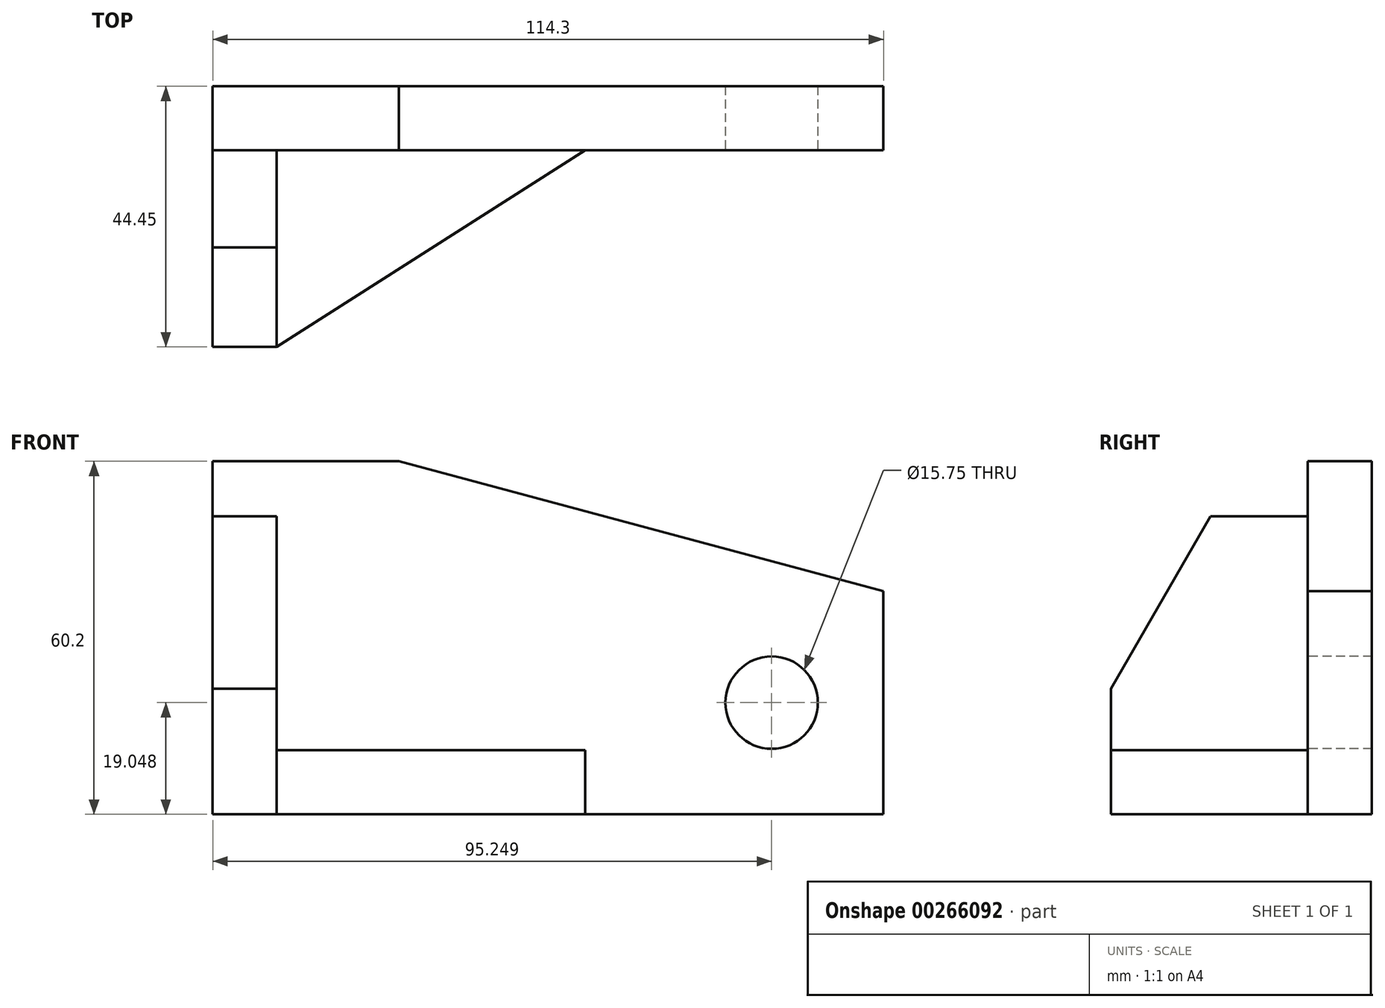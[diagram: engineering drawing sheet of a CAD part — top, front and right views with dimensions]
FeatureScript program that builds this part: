
annotation { "Feature Type Name" : "Feature", "Feature Type Description" : "" }
export const myFeature = defineFeature(function(context is Context, id is Id, definition is map)
    precondition{}
    {
        {
            var Q0;
            Q0=qCreatedBy(makeId("Front.planeOp"),FACE);
            var sketch = newSketch(context, id + "F0", { "sketchPlane" : qUnion([Q0])});
            skLineSegment(sketch, "E0.bottom", {"start": v(-55.92, 20.43) * mm, "end": v(58.38, 20.43) * mm});
            skLineSegment(sketch, "E0.top", {"start": v(-55.92, -39.77) * mm, "end": v(58.38, -39.77) * mm});
            skLineSegment(sketch, "E0.left", {"start": v(-55.92, 20.43) * mm, "end": v(-55.92, -39.77) * mm});
            skLineSegment(sketch, "E0.right", {"start": v(58.38, 20.43) * mm, "end": v(58.38, -39.77) * mm});
            skSolve(sketch);
        }
        {
            var Q0;
            Q0 = qSketchRegion(id + "F0", true);
            extrude(context, id + "F1", {"entities" : qUnion([Q0]), "depth" : 10.92 * mm});
        }
        {
            var Q0;
            Q0=makeQuery(id+"F1.opExtrude","CAP_FACE",FACE,{"disambiguationData":[OSD([sQuery(id+"F0.wireOp",EDGE,"E0.bottom"),sQuery(id+"F0.wireOp",EDGE,"E0.top"),sQuery(id+"F0.wireOp",EDGE,"E0.left"),sQuery(id+"F0.wireOp",EDGE,"E0.right")])],"isStart":false});
            var sketch = newSketch(context, id + "F2", { "sketchPlane" : qUnion([Q0])});
            skLineSegment(sketch, "E1", {"start": v(58.38, 20.43) * mm, "end": v(-24.17, 20.43) * mm});
            skLineSegment(sketch, "E2", {"start": v(58.38, 20.43) * mm, "end": v(58.38, -1.7) * mm});
            skLineSegment(sketch, "E3", {"start": v(58.38, -1.7) * mm, "end": v(-24.17, 20.43) * mm});
            skSolve(sketch);
        }
        {
            var Q0;
            Q0=makeQuery(id+"F2.imprint","IMPRINT",FACE,{"disambiguationData":[TD([[makeQuery(id+"F2.imprint","IMPRINT",EDGE,{"derivedFrom":sQuery(id+"F2.wireOp",EDGE,"E1")}),-1.0]])]});
            extrude(context, id + "F3", {"entities" : qUnion([Q0]), "operationType" : NewBodyOperationType.REMOVE, "oppositeDirection" : true, "depth" : 10.92 * mm});
        }
        {
            var Q0;
            Q0=makeQuery(id+"F1.opExtrude","CAP_FACE",FACE,{"disambiguationData":[OSD([sQuery(id+"F0.wireOp",EDGE,"E0.bottom"),sQuery(id+"F0.wireOp",EDGE,"E0.top"),sQuery(id+"F0.wireOp",EDGE,"E0.left"),sQuery(id+"F0.wireOp",EDGE,"E0.right")])],"isStart":false});
            var sketch = newSketch(context, id + "F4", { "sketchPlane" : qUnion([Q0])});
            skLineSegment(sketch, "E4", {"start": v(58.38, -39.77) * mm, "end": v(39.33, -39.77) * mm});
            skLineSegment(sketch, "E5", {"start": v(39.33, -39.77) * mm, "end": v(58.38, -39.77) * mm});
            skLineSegment(sketch, "E6", {"start": v(39.33, -39.77) * mm, "end": v(39.33, -20.72) * mm});
            skCircle(sketch, "E7", {"center": v(39.33, -20.72) * mm, "radius": 7.87 * mm});
            skSolve(sketch);
        }
        {
            var Q0;
            Q0=makeQuery(id+"F4.imprint","IMPRINT",FACE,{"disambiguationData":[TD([[makeQuery(id+"F4.imprint","IMPRINT",EDGE,{"derivedFrom":sQuery(id+"F4.wireOp",EDGE,"E7")}),1.0]])]});
            extrude(context, id + "F5", {"entities" : qUnion([Q0]), "operationType" : NewBodyOperationType.REMOVE, "oppositeDirection" : true, "depth" : 10.92 * mm});
        }
        {
            var Q0;
            Q0=makeQuery(id+"F1.opExtrude","CAP_FACE",FACE,{"disambiguationData":[OSD([sQuery(id+"F0.wireOp",EDGE,"E0.bottom"),sQuery(id+"F0.wireOp",EDGE,"E0.top"),sQuery(id+"F0.wireOp",EDGE,"E0.left"),sQuery(id+"F0.wireOp",EDGE,"E0.right")])],"isStart":false});
            var sketch = newSketch(context, id + "F6", { "sketchPlane" : qUnion([Q0])});
            skLineSegment(sketch, "E8.bottom", {"start": v(-55.92, 11.03) * mm, "end": v(7.58, 11.03) * mm});
            skLineSegment(sketch, "E8.top", {"start": v(-55.92, -39.77) * mm, "end": v(7.58, -39.77) * mm});
            skLineSegment(sketch, "E8.left", {"start": v(-55.92, 11.03) * mm, "end": v(-55.92, -39.77) * mm});
            skLineSegment(sketch, "E8.right", {"start": v(7.58, 11.03) * mm, "end": v(7.58, -39.77) * mm});
            skSolve(sketch);
        }
        {
            var Q0;
            Q0=makeQuery(id+"F6.imprint","IMPRINT",FACE,{"disambiguationData":[TD([[makeQuery(id+"F6.imprint","IMPRINT",EDGE,{"derivedFrom":sQuery(id+"F6.wireOp",EDGE,"E8.bottom")}),-1.0]])]});
            extrude(context, id + "F7", {"entities" : qUnion([Q0]), "operationType" : NewBodyOperationType.ADD, "depth" : 33.53 * mm});
        }
        {
            var Q0;
            Q0=makeQuery(id+"F7.opExtrude","CAP_FACE",FACE,{"disambiguationData":[OSD([sQuery(id+"F6.wireOp",EDGE,"E8.bottom"),sQuery(id+"F6.wireOp",EDGE,"E8.top"),sQuery(id+"F6.wireOp",EDGE,"E8.left"),sQuery(id+"F6.wireOp",EDGE,"E8.right")])],"isStart":false});
            var sketch = newSketch(context, id + "F8", { "sketchPlane" : qUnion([Q0])});
            skLineSegment(sketch, "E9.bottom", {"start": v(-45, 11.03) * mm, "end": v(7.58, 11.03) * mm});
            skLineSegment(sketch, "E9.top", {"start": v(-45, -28.85) * mm, "end": v(7.58, -28.85) * mm});
            skLineSegment(sketch, "E9.left", {"start": v(-45, 11.03) * mm, "end": v(-45, -28.85) * mm});
            skLineSegment(sketch, "E9.right", {"start": v(7.58, 11.03) * mm, "end": v(7.58, -28.85) * mm});
            skSolve(sketch);
        }
        {
            var Q0;
            Q0=makeQuery(id+"F8.imprint","IMPRINT",FACE,{"disambiguationData":[TD([[makeQuery(id+"F8.imprint","IMPRINT",EDGE,{"derivedFrom":sQuery(id+"F8.wireOp",EDGE,"E9.bottom")}),-1.0]])]});
            extrude(context, id + "F9", {"entities" : qUnion([Q0]), "operationType" : NewBodyOperationType.REMOVE, "oppositeDirection" : true, "depth" : 33.53 * mm});
        }
        {
            var Q0;
            Q0=makeQuery(id+"F9.boolean.opBoolean","COPY",FACE,{"derivedFrom":makeQuery(id+"F9.opExtrude","SWEPT_FACE",FACE,{"disambiguationData":[OSD([sQuery(id+"F8.wireOp",EDGE,"E9.top")])]})});
            var sketch = newSketch(context, id + "F10", { "sketchPlane" : qUnion([Q0])});
            skLineSegment(sketch, "E10", {"start": v(-45, -44.45) * mm, "end": v(7.58, -10.92) * mm});
            skSolve(sketch);
        }
        {
            var Q0;
            Q0=makeQuery(id+"F10.imprint","IMPRINT",FACE,{"disambiguationData":[TD([[makeQuery(id+"F10.imprint","IMPRINT",EDGE,{"derivedFrom":sQuery(id+"F10.wireOp",EDGE,"E10")}),-1.0]])]});
            extrude(context, id + "F11", {"entities" : qUnion([Q0]), "operationType" : NewBodyOperationType.REMOVE, "oppositeDirection" : true, "depth" : 10.92 * mm});
        }
        {
            var Q0;
            Q0=makeQuery(id+"F9.boolean.opBoolean","COPY",FACE,{"derivedFrom":makeQuery(id+"F9.opExtrude","SWEPT_FACE",FACE,{"disambiguationData":[OSD([sQuery(id+"F8.wireOp",EDGE,"E9.left")])]})});
            var sketch = newSketch(context, id + "F12", { "sketchPlane" : qUnion([Q0])});
            skLineSegment(sketch, "E11", {"start": v(-44.45, -40.47) * mm, "end": v(-44.45, -18.37) * mm});
            skLineSegment(sketch, "E12", {"start": v(-44.45, -18.37) * mm, "end": v(-44.45, 11.03) * mm});
            skLineSegment(sketch, "E13", {"start": v(-44.45, -18.37) * mm, "end": v(-27.48, 11.03) * mm});
            skLineSegment(sketch, "E14", {"start": v(-27.48, 11.03) * mm, "end": v(-44.45, 11.03) * mm});
            skSolve(sketch);
        }
        {
            var Q0;
            Q0=makeQuery(id+"F12.imprint","IMPRINT",FACE,{"disambiguationData":[TD([[makeQuery(id+"F12.imprint","IMPRINT",EDGE,{"derivedFrom":sQuery(id+"F12.wireOp",EDGE,"E12")}),1.0]])]});
            extrude(context, id + "F13", {"entities" : qUnion([Q0]), "operationType" : NewBodyOperationType.REMOVE, "oppositeDirection" : true, "depth" : 10.92 * mm});
        }
    });
